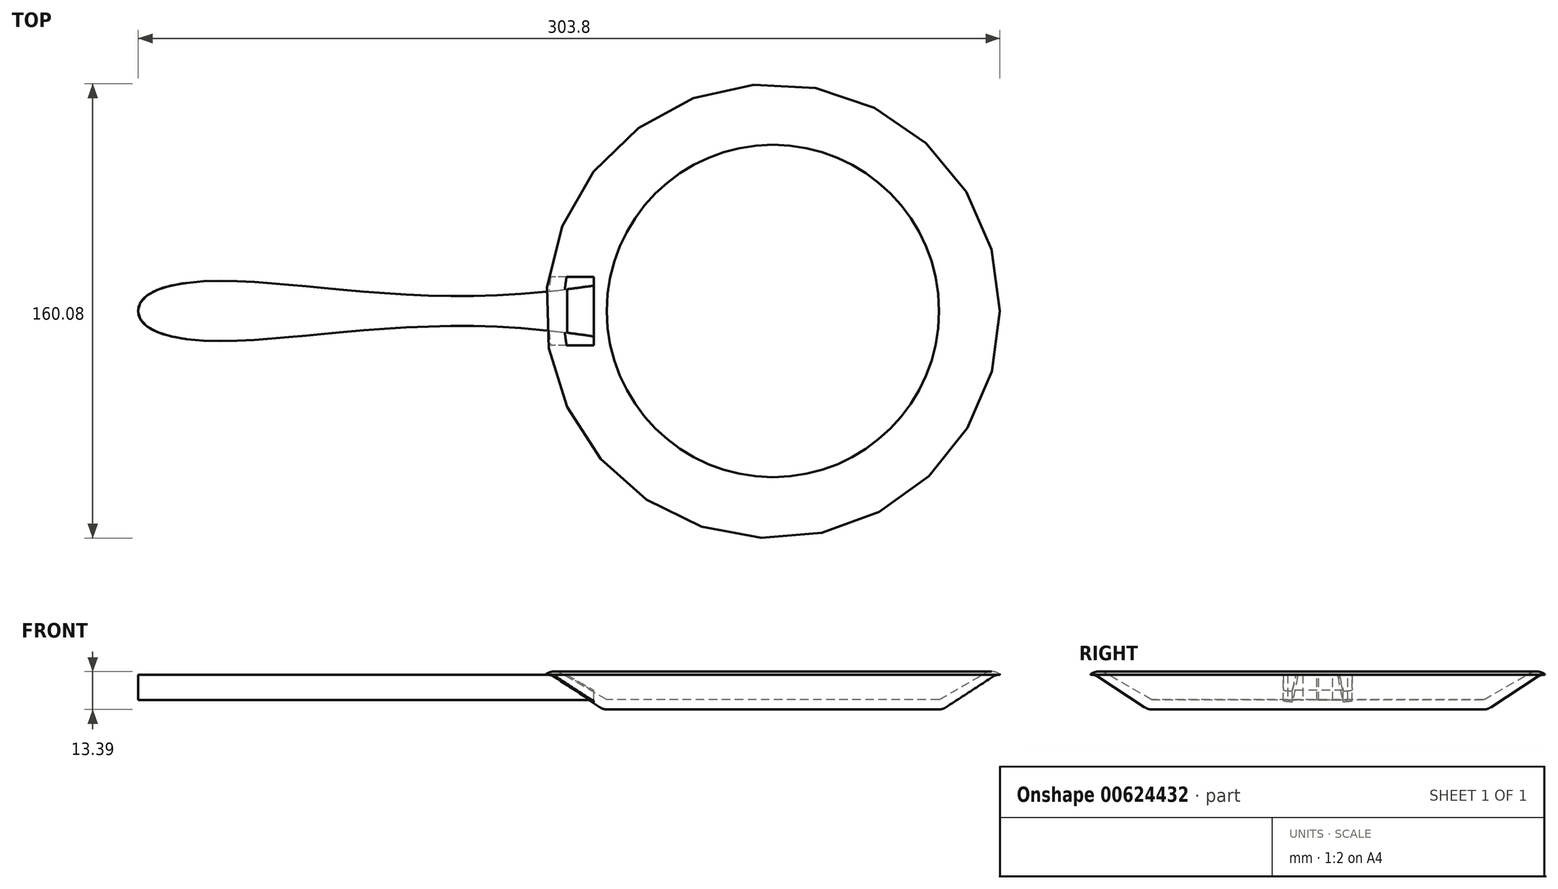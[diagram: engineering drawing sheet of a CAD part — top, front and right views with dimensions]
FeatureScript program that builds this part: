
annotation { "Feature Type Name" : "Feature", "Feature Type Description" : "" }
export const myFeature = defineFeature(function(context is Context, id is Id, definition is map)
    precondition{}
    {
        {
            var Q0;
            Q0=qCreatedBy(makeId("Front.planeOp"),FACE);
            var sketch = newSketch(context, id + "F0", { "sketchPlane" : qUnion([Q0])});
            skLineSegment(sketch, "E0", {"start": v(0, -12.2) * mm, "end": v(-58.32, -12.2) * mm});
            skLineSegment(sketch, "E1", {"start": v(-61.1, -11.38) * mm, "end": v(-77.55, -0.63) * mm});
            skPoint(sketch, "E2.visualSharp", {"position": v(-59.84, -12.2) * mm});
            skArc(sketch, "E2.filletArc", {"start": v(-61.1, -11.38) * mm, "mid": v(-59.77, -12) * mm, "end": v(-58.32, -12.2) * mm});
            skArc(sketch, "E3", {"start": v(-77.55, -0.63) * mm, "mid": v(-78.68, -0.11) * mm, "end": v(-79.9, 0.04) * mm});
            skArc(sketch, "E4", {"start": v(-74.61, 0.51) * mm, "mid": v(-77.33, 1.17) * mm, "end": v(-79.98, 0.27) * mm});
            skLineSegment(sketch, "E5", {"start": v(-74.61, 0.51) * mm, "end": v(-58.57, -8.75) * mm});
            skPoint(sketch, "E6.visualSharp", {"position": v(-80.33, 0) * mm});
            skArc(sketch, "E6.filletArc", {"start": v(-79.98, 0.27) * mm, "mid": v(-80.03, 0.12) * mm, "end": v(-79.9, 0.04) * mm});
            skLineSegment(sketch, "E7", {"start": v(-58.57, -8.75) * mm, "end": v(0, -8.75) * mm});
            skLineSegment(sketch, "E8", {"start": v(0, -8.75) * mm, "end": v(0, -12.2) * mm});
            skSolve(sketch);
        }
        {
            var Q0;
            Q0=makeQuery(id+"F0.imprint","IMPRINT",FACE,{"disambiguationData":[TD([[makeQuery(id+"F0.imprint","IMPRINT",EDGE,{"derivedFrom":sQuery(id+"F0.wireOp",EDGE,"E0")}),-1.0]])]});
            var Q1;
            Q1=sQuery(id+"F0.wireOp",EDGE,"E8");
            revolve(context, id + "F1", {"entities" : qUnion([Q0]), "axis" : qUnion([Q1]), "revolveType" : RevolveType.FULL});
        }
        {
            var Q0;
            Q0=qCreatedBy(makeId("Top.planeOp"),FACE);
            var sketch = newSketch(context, id + "F2", { "sketchPlane" : qUnion([Q0])});
            skLineSegment(sketch, "E9", {"start": v(-35.23, 0) * mm, "end": v(-362.14, 0) * mm});
            skLineSegment(sketch, "E10.bottom", {"start": v(-63.15, 12.07) * mm, "end": v(-223.76, 12.07) * mm});
            skLineSegment(sketch, "E10.top", {"start": v(-63.15, -12.07) * mm, "end": v(-223.76, -12.07) * mm});
            skLineSegment(sketch, "E10.left", {"start": v(-63.15, 12.07) * mm, "end": v(-63.15, -12.07) * mm});
            skLineSegment(sketch, "E10.right", {"start": v(-223.76, 12.07) * mm, "end": v(-223.76, -12.07) * mm});
            skSolve(sketch);
        }
        {
            var Q0;
            Q0=qSketchRegion(id+"F2",true);
            extrude(context, id + "F3", {"entities" : qUnion([Q0]), "oppositeDirection" : true, "depth" : 8.9 * mm, "offsetDistance" : 25.4 * mm});
        }
        {
            var Q0;
            Q0=makeQuery(id+"F3.opExtrude","CAP_FACE",FACE,{"disambiguationData":[OSD([sQuery(id+"F2.wireOp",EDGE,"E10.bottom"),sQuery(id+"F2.wireOp",EDGE,"E10.top"),sQuery(id+"F2.wireOp",EDGE,"E10.left"),sQuery(id+"F2.wireOp",EDGE,"E10.right")])],"isStart":true});
            var sketch = newSketch(context, id + "F4", { "sketchPlane" : qUnion([Q0])});
            skFitSpline(sketch, "E11", {"points": [v(-223.76, 0) * mm, v(-221.07, 5.14) * mm, v(-205.39, 10.06) * mm, v(-180.89, 10.06) * mm, v(-154.26, 7.72) * mm, v(-116.01, 5.3) * mm, v(-63.15, 8.95) * mm], "startDerivative": vector(-1.88, 60.75) * mm, "endDerivative": vector(257.35, 38.26) * mm});
            skFitSpline(sketch, "E12.MirrorCS", {"points": [v(-223.76, 0) * mm, v(-221.07, -5.14) * mm, v(-205.39, -10.06) * mm, v(-180.89, -10.06) * mm, v(-154.26, -7.72) * mm, v(-116.01, -5.3) * mm, v(-63.15, -8.95) * mm], "startDerivative": vector(-1.88, -60.75) * mm, "endDerivative": vector(257.35, -38.26) * mm});
            skLineSegment(sketch, "E13.bottom", {"start": v(-223.76, -12.07) * mm, "end": v(-63.15, -12.07) * mm});
            skLineSegment(sketch, "E13.top", {"start": v(-223.76, 12.07) * mm, "end": v(-63.15, 12.07) * mm});
            skLineSegment(sketch, "E13.left", {"start": v(-223.76, -12.07) * mm, "end": v(-223.76, 12.07) * mm});
            skLineSegment(sketch, "E13.right", {"start": v(-63.15, -12.07) * mm, "end": v(-63.15, -8.95) * mm});
            skLineSegment(sketch, "E14.trimOffspring", {"start": v(-63.15, 8.95) * mm, "end": v(-63.15, 12.07) * mm});
            skSolve(sketch);
        }
        {
            var Q0;
            {var subQ4=sQuery(id+"F4.wireOp",EDGE,"E13.bottom");Q0=makeQuery(id+"F4.imprint","IMPRINT",FACE,{"disambiguationData":[TD([[makeQuery(id+"F4.imprint","IMPRINT",EDGE,{"derivedFrom":subQ4}),-1.0]])]});}
            var Q1;
            {var subQ4=sQuery(id+"F4.wireOp",EDGE,"E13.top");Q1=makeQuery(id+"F4.imprint","IMPRINT",FACE,{"disambiguationData":[TD([[makeQuery(id+"F4.imprint","IMPRINT",EDGE,{"derivedFrom":subQ4}),1.0]])]});}
            extrude(context, id + "F5", {"entities" : qUnion([Q0, Q1]), "operationType" : NewBodyOperationType.REMOVE, "oppositeDirection" : true, "depth" : 25.4 * mm, "offsetDistance" : 25.4 * mm});
        }
        {
            var Q0;
            Q0=makeQuery(id+"F3.opExtrude","CAP_EDGE",EDGE,{"disambiguationData":[OSD([sQuery(id+"F2.wireOp",EDGE,"E10.left")])],"isStart":true});
            chamfer(context, id + "F6", {"entities" : qUnion([Q0]), "chamferType" : ChamferType.OFFSET_ANGLE, "width" : 9.4 * mm, "oppositeDirection" : true, "angle" : 30 * degree, "tangentPropagation" : true});
        }
    });
